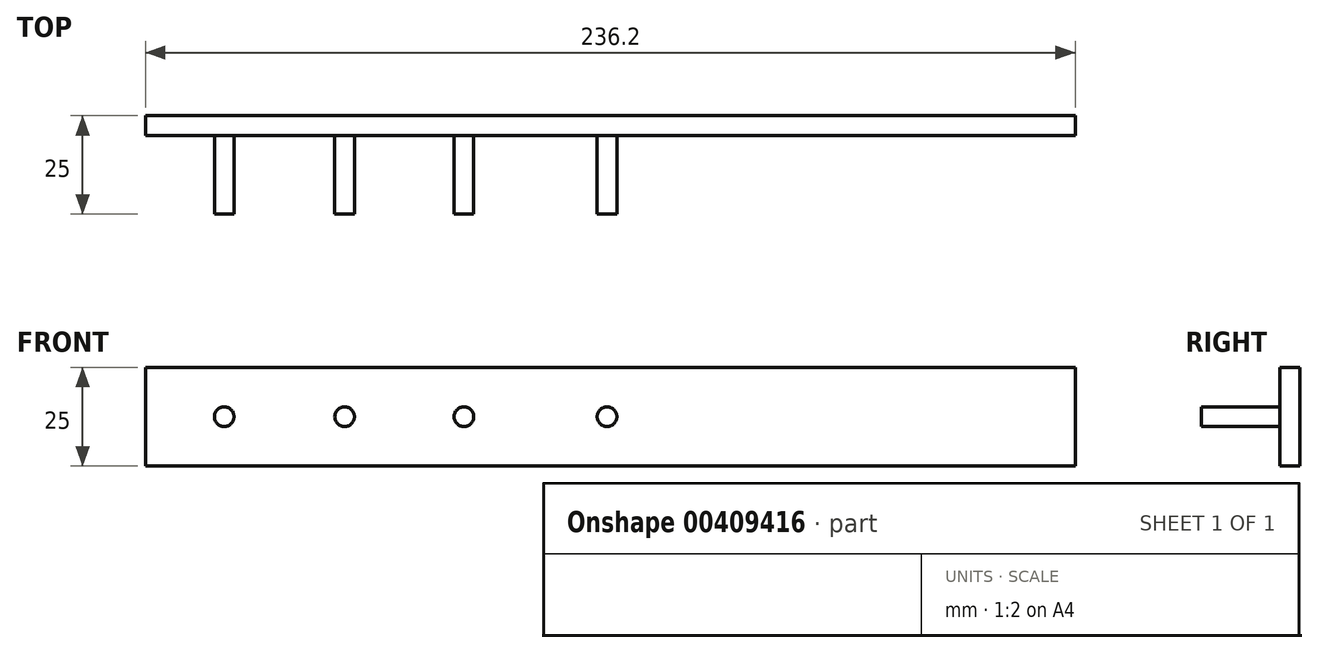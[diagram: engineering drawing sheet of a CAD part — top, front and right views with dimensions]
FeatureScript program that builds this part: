
annotation { "Feature Type Name" : "Feature", "Feature Type Description" : "" }
export const myFeature = defineFeature(function(context is Context, id is Id, definition is map)
    precondition{}
    {
        {
            var Q0;
            Q0=qCreatedBy(makeId("Front.planeOp"),FACE);
            var sketch = newSketch(context, id + "F0", { "sketchPlane" : qUnion([Q0])});
            skLineSegment(sketch, "E0.bottom", {"start": v(0, 0) * mm, "end": v(236.2, 0) * mm});
            skLineSegment(sketch, "E0.top", {"start": v(0, 25) * mm, "end": v(236.2, 25) * mm});
            skLineSegment(sketch, "E0.left", {"start": v(0, 0) * mm, "end": v(0, 25) * mm});
            skLineSegment(sketch, "E0.right", {"start": v(236.2, 0) * mm, "end": v(236.2, 25) * mm});
            skSolve(sketch);
        }
        {
            var Q0;
            Q0 = qSketchRegion(id + "F0", true);
            extrude(context, id + "F1", {"entities" : qUnion([Q0]), "oppositeDirection" : true, "depth" : 5 * mm});
        }
        {
            var Q0;
            Q0=makeQuery(id+"F1.opExtrude","CAP_FACE",FACE,{"disambiguationData":[OSD([sQuery(id+"F0.wireOp",EDGE,"E0.bottom"),sQuery(id+"F0.wireOp",EDGE,"E0.top"),sQuery(id+"F0.wireOp",EDGE,"E0.left"),sQuery(id+"F0.wireOp",EDGE,"E0.right")])],"isStart":true});
            var sketch = newSketch(context, id + "F2", { "sketchPlane" : qUnion([Q0])});
            skCircle(sketch, "E1", {"center": v(19.98, 12.5) * mm, "radius": 2.5 * mm});
            skPoint(sketch, "E1.centerSnap0", {"position": v(0, 12.5) * mm});
            skCircle(sketch, "E2", {"center": v(50.58, 12.5) * mm, "radius": 2.5 * mm});
            skCircle(sketch, "E3", {"center": v(80.88, 12.5) * mm, "radius": 2.5 * mm});
            skCircle(sketch, "E4", {"center": v(117.24, 12.5) * mm, "radius": 2.5 * mm});
            skSolve(sketch);
        }
        {
            var Q0;
            Q0 = qSketchRegion(id + "F2", true);
            extrude(context, id + "F3", {"entities" : qUnion([Q0]), "operationType" : NewBodyOperationType.ADD, "depth" : 20 * mm});
        }
    });
